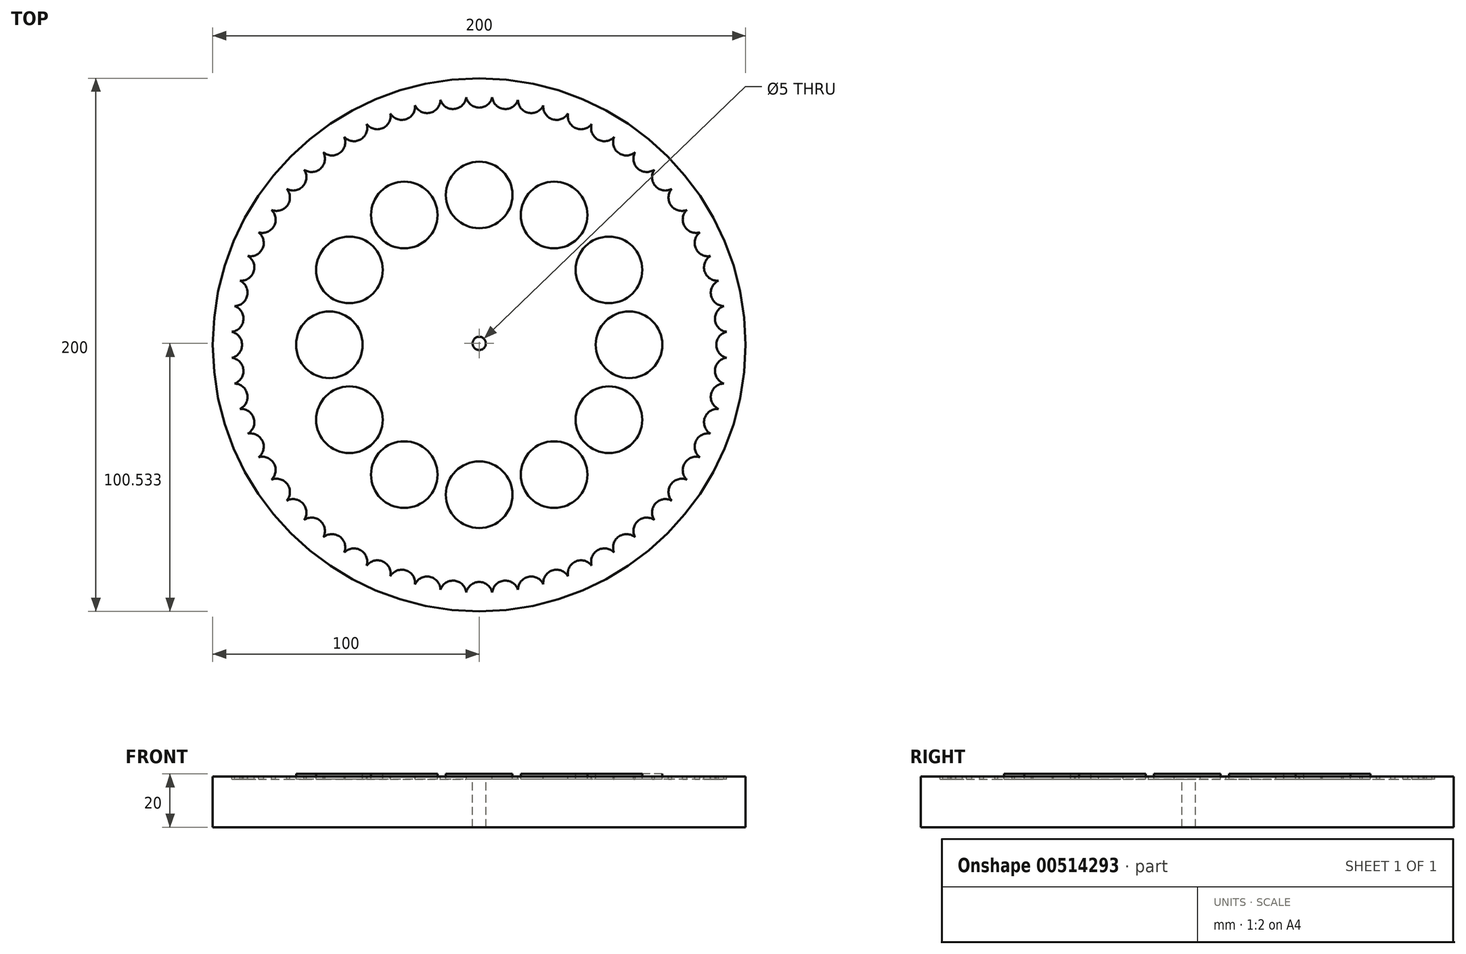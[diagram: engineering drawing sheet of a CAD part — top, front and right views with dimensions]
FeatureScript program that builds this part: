
annotation { "Feature Type Name" : "Feature", "Feature Type Description" : "" }
export const myFeature = defineFeature(function(context is Context, id is Id, definition is map)
    precondition{}
    {
        {
            var Q0;
            Q0=qCreatedBy(makeId("Top.planeOp"),FACE);
            var sketch = newSketch(context, id + "F0", { "sketchPlane" : qUnion([Q0])});
            skCircle(sketch, "E0", {"center": v(0, 0) * mm, "radius": 100 * mm});
            skSolve(sketch);
        }
        {
            var Q0;
            Q0=makeQuery(id+"F0.imprint","IMPRINT",FACE,{"disambiguationData":[TD([[makeQuery(id+"F0.imprint","IMPRINT",EDGE,{"derivedFrom":sQuery(id+"F0.wireOp",EDGE,"E0")}),1.0]])]});
            extrude(context, id + "F1", {"entities" : qUnion([Q0]), "oppositeDirection" : true, "depth" : 20 * mm});
        }
        {
            var Q0;
            Q0=makeQuery(id+"F1.opExtrude","CAP_FACE",FACE,{"disambiguationData":[OSD([sQuery(id+"F0.wireOp",EDGE,"E0")])],"isStart":true});
            var sketch = newSketch(context, id + "F2", { "sketchPlane" : qUnion([Q0])});
            skText(sketch, "E1", { "text": "12\n00", "fontName": "NotoSans-Regular.ttf"});
            skCircle(sketch, "E2", {"center": v(0, 56.24) * mm, "radius": 12.5 * mm});
            skCircle(sketch, "E3.1.0", {"center": v(-28.12, 48.7) * mm, "radius": 12.5 * mm});
            skCircle(sketch, "E3.2.0", {"center": v(-48.7, 28.12) * mm, "radius": 12.5 * mm});
            skCircle(sketch, "E3.3.0", {"center": v(-56.24, 0) * mm, "radius": 12.5 * mm});
            skCircle(sketch, "E3.4.0", {"center": v(-48.7, -28.12) * mm, "radius": 12.5 * mm});
            skCircle(sketch, "E3.5.0", {"center": v(-28.12, -48.7) * mm, "radius": 12.5 * mm});
            skCircle(sketch, "E3.6.0", {"center": v(0, -56.24) * mm, "radius": 12.5 * mm});
            skCircle(sketch, "E3.7.0", {"center": v(28.12, -48.7) * mm, "radius": 12.5 * mm});
            skCircle(sketch, "E3.8.0", {"center": v(48.7, -28.12) * mm, "radius": 12.5 * mm});
            skCircle(sketch, "E3.9.0", {"center": v(56.24, 0) * mm, "radius": 12.5 * mm});
            skCircle(sketch, "E3.10.0", {"center": v(48.7, 28.12) * mm, "radius": 12.5 * mm});
            skCircle(sketch, "E3.11.0", {"center": v(28.12, 48.7) * mm, "radius": 12.5 * mm});
            skPoint(sketch, "E3.center", {"position": v(0, 0) * mm});
            const initialGuessF2  = {"E1": [-0.00645, 0.06, 1, 0, 0.008]};
            skSetInitialGuess(sketch, initialGuessF2);
            skSolve(sketch);
        }
        {
            var Q0;
            Q0=makeQuery(id+"F2.imprint","IMPRINT",FACE,{"disambiguationData":[TD([[makeQuery(id+"F2.imprint","IMPRINT",EDGE,{"derivedFrom":sQuery(id+"F2.wireOp",EDGE,"E2")}),-1.0]])]});
            extrude(context, id + "F3", {"entities" : qUnion([Q0]), "operationType" : NewBodyOperationType.REMOVE, "oppositeDirection" : true, "depth" : 1 * mm});
        }
        {
            var Q0;
            Q0=makeQuery(id+"F3.boolean.opBoolean","COPY",FACE,{"derivedFrom":makeQuery(id+"F3.opExtrude","CAP_FACE",FACE,{"disambiguationData":[OSD([sQuery(id+"F0.wireOp",EDGE,"E0"),sQuery(id+"F2.wireOp",EDGE,"E2"),sQuery(id+"F2.wireOp",EDGE,"E3.1.0"),sQuery(id+"F2.wireOp",EDGE,"E3.2.0"),sQuery(id+"F2.wireOp",EDGE,"E3.3.0"),sQuery(id+"F2.wireOp",EDGE,"E3.4.0"),sQuery(id+"F2.wireOp",EDGE,"E3.5.0"),sQuery(id+"F2.wireOp",EDGE,"E3.6.0"),sQuery(id+"F2.wireOp",EDGE,"E3.7.0"),sQuery(id+"F2.wireOp",EDGE,"E3.8.0"),sQuery(id+"F2.wireOp",EDGE,"E3.9.0"),sQuery(id+"F2.wireOp",EDGE,"E3.10.0"),sQuery(id+"F2.wireOp",EDGE,"E3.11.0")])],"isStart":false})});
            var sketch = newSketch(context, id + "F4", { "sketchPlane" : qUnion([Q0])});
            skCircle(sketch, "E4", {"center": v(0, 94) * mm, "radius": 5 * mm});
            skCircle(sketch, "E5.1.0", {"center": v(-9.83, 93.49) * mm, "radius": 5 * mm});
            skCircle(sketch, "E5.2.0", {"center": v(-19.54, 91.95) * mm, "radius": 5 * mm});
            skCircle(sketch, "E5.3.0", {"center": v(-29.05, 89.4) * mm, "radius": 5 * mm});
            skCircle(sketch, "E5.4.0", {"center": v(-38.23, 85.87) * mm, "radius": 5 * mm});
            skCircle(sketch, "E5.5.0", {"center": v(-47, 81.4) * mm, "radius": 5 * mm});
            skCircle(sketch, "E5.6.0", {"center": v(-55.25, 76.05) * mm, "radius": 5 * mm});
            skCircle(sketch, "E5.7.0", {"center": v(-62.9, 69.86) * mm, "radius": 5 * mm});
            skCircle(sketch, "E5.8.0", {"center": v(-69.86, 62.9) * mm, "radius": 5 * mm});
            skCircle(sketch, "E5.9.0", {"center": v(-76.05, 55.25) * mm, "radius": 5 * mm});
            skCircle(sketch, "E5.10.0", {"center": v(-81.4, 47) * mm, "radius": 5 * mm});
            skCircle(sketch, "E5.11.0", {"center": v(-85.87, 38.23) * mm, "radius": 5 * mm});
            skCircle(sketch, "E5.12.0", {"center": v(-89.4, 29.05) * mm, "radius": 5 * mm});
            skCircle(sketch, "E5.13.0", {"center": v(-91.95, 19.54) * mm, "radius": 5 * mm});
            skCircle(sketch, "E5.14.0", {"center": v(-93.49, 9.83) * mm, "radius": 5 * mm});
            skCircle(sketch, "E5.15.0", {"center": v(-94, 0) * mm, "radius": 5 * mm});
            skCircle(sketch, "E5.16.0", {"center": v(-93.49, -9.83) * mm, "radius": 5 * mm});
            skCircle(sketch, "E5.17.0", {"center": v(-91.95, -19.54) * mm, "radius": 5 * mm});
            skCircle(sketch, "E5.18.0", {"center": v(-89.4, -29.05) * mm, "radius": 5 * mm});
            skCircle(sketch, "E5.19.0", {"center": v(-85.87, -38.23) * mm, "radius": 5 * mm});
            skCircle(sketch, "E5.20.0", {"center": v(-81.4, -47) * mm, "radius": 5 * mm});
            skCircle(sketch, "E5.21.0", {"center": v(-76.05, -55.25) * mm, "radius": 5 * mm});
            skCircle(sketch, "E5.22.0", {"center": v(-69.86, -62.9) * mm, "radius": 5 * mm});
            skCircle(sketch, "E5.23.0", {"center": v(-62.9, -69.86) * mm, "radius": 5 * mm});
            skCircle(sketch, "E5.24.0", {"center": v(-55.25, -76.05) * mm, "radius": 5 * mm});
            skCircle(sketch, "E5.25.0", {"center": v(-47, -81.4) * mm, "radius": 5 * mm});
            skCircle(sketch, "E5.26.0", {"center": v(-38.23, -85.87) * mm, "radius": 5 * mm});
            skCircle(sketch, "E5.27.0", {"center": v(-29.05, -89.4) * mm, "radius": 5 * mm});
            skCircle(sketch, "E5.28.0", {"center": v(-19.54, -91.95) * mm, "radius": 5 * mm});
            skCircle(sketch, "E5.29.0", {"center": v(-9.83, -93.49) * mm, "radius": 5 * mm});
            skCircle(sketch, "E5.30.0", {"center": v(0, -94) * mm, "radius": 5 * mm});
            skCircle(sketch, "E5.31.0", {"center": v(9.83, -93.49) * mm, "radius": 5 * mm});
            skCircle(sketch, "E5.32.0", {"center": v(19.54, -91.95) * mm, "radius": 5 * mm});
            skCircle(sketch, "E5.33.0", {"center": v(29.05, -89.4) * mm, "radius": 5 * mm});
            skCircle(sketch, "E5.34.0", {"center": v(38.23, -85.87) * mm, "radius": 5 * mm});
            skCircle(sketch, "E5.35.0", {"center": v(47, -81.4) * mm, "radius": 5 * mm});
            skCircle(sketch, "E5.36.0", {"center": v(55.25, -76.05) * mm, "radius": 5 * mm});
            skCircle(sketch, "E5.37.0", {"center": v(62.9, -69.86) * mm, "radius": 5 * mm});
            skCircle(sketch, "E5.38.0", {"center": v(69.86, -62.9) * mm, "radius": 5 * mm});
            skCircle(sketch, "E5.39.0", {"center": v(76.05, -55.25) * mm, "radius": 5 * mm});
            skCircle(sketch, "E5.40.0", {"center": v(81.4, -47) * mm, "radius": 5 * mm});
            skCircle(sketch, "E5.41.0", {"center": v(85.87, -38.23) * mm, "radius": 5 * mm});
            skCircle(sketch, "E5.42.0", {"center": v(89.4, -29.05) * mm, "radius": 5 * mm});
            skCircle(sketch, "E5.43.0", {"center": v(91.95, -19.54) * mm, "radius": 5 * mm});
            skCircle(sketch, "E5.44.0", {"center": v(93.49, -9.83) * mm, "radius": 5 * mm});
            skCircle(sketch, "E5.45.0", {"center": v(94, 0) * mm, "radius": 5 * mm});
            skCircle(sketch, "E5.46.0", {"center": v(93.49, 9.83) * mm, "radius": 5 * mm});
            skCircle(sketch, "E5.47.0", {"center": v(91.95, 19.54) * mm, "radius": 5 * mm});
            skCircle(sketch, "E5.48.0", {"center": v(89.4, 29.05) * mm, "radius": 5 * mm});
            skCircle(sketch, "E5.49.0", {"center": v(85.87, 38.23) * mm, "radius": 5 * mm});
            skCircle(sketch, "E5.50.0", {"center": v(81.4, 47) * mm, "radius": 5 * mm});
            skCircle(sketch, "E5.51.0", {"center": v(76.05, 55.25) * mm, "radius": 5 * mm});
            skCircle(sketch, "E5.52.0", {"center": v(69.86, 62.9) * mm, "radius": 5 * mm});
            skCircle(sketch, "E5.53.0", {"center": v(62.9, 69.86) * mm, "radius": 5 * mm});
            skCircle(sketch, "E5.54.0", {"center": v(55.25, 76.05) * mm, "radius": 5 * mm});
            skCircle(sketch, "E5.55.0", {"center": v(47, 81.4) * mm, "radius": 5 * mm});
            skCircle(sketch, "E5.56.0", {"center": v(38.23, 85.87) * mm, "radius": 5 * mm});
            skCircle(sketch, "E5.57.0", {"center": v(29.05, 89.4) * mm, "radius": 5 * mm});
            skCircle(sketch, "E5.58.0", {"center": v(19.54, 91.95) * mm, "radius": 5 * mm});
            skCircle(sketch, "E5.59.0", {"center": v(9.83, 93.49) * mm, "radius": 5 * mm});
            skPoint(sketch, "E5.center", {"position": v(0, 0) * mm});
            skSolve(sketch);
        }
        {
            var Q0;
            Q0=makeQuery(id+"F4.imprint","IMPRINT",FACE,{"disambiguationData":[TD([[makeQuery(id+"F4.imprint","IMPRINT",EDGE,{"derivedFrom":makeQuery(id+"F3.boolean.opBoolean","COPY",EDGE,{"derivedFrom":makeQuery(id+"F3.opExtrude","CAP_EDGE",EDGE,{"disambiguationData":[OSD([sQuery(id+"F2.wireOp",EDGE,"E2")])],"isStart":false})})}),-1.0]])]});
            var Q1;
            Q1=makeQuery(id+"F4.imprint","IMPRINT",FACE,{"disambiguationData":[TD([[makeQuery(id+"F4.imprint","IMPRINT",EDGE,{"derivedFrom":makeQuery(id+"F3.boolean.opBoolean","COPY",EDGE,{"derivedFrom":makeQuery(id+"F3.opExtrude","CAP_EDGE",EDGE,{"disambiguationData":[OSD([sQuery(id+"F0.wireOp",EDGE,"E0")])],"isStart":false})})}),1.0]])]});
            extrude(context, id + "F5", {"entities" : qUnion([Q0, Q1]), "operationType" : NewBodyOperationType.REMOVE, "oppositeDirection" : true, "depth" : 1 * mm});
        }
        {
            var Q0;
            Q0=makeQuery(id+"F5.boolean.opBoolean","COPY",FACE,{"derivedFrom":makeQuery(id+"F5.opExtrude","CAP_FACE",FACE,{"disambiguationData":[OSD([sQuery(id+"F2.wireOp",EDGE,"E2"),sQuery(id+"F2.wireOp",EDGE,"E3.1.0"),sQuery(id+"F2.wireOp",EDGE,"E3.2.0"),sQuery(id+"F2.wireOp",EDGE,"E3.3.0"),sQuery(id+"F2.wireOp",EDGE,"E3.4.0"),sQuery(id+"F2.wireOp",EDGE,"E3.5.0"),sQuery(id+"F2.wireOp",EDGE,"E3.6.0"),sQuery(id+"F2.wireOp",EDGE,"E3.7.0"),sQuery(id+"F2.wireOp",EDGE,"E3.8.0"),sQuery(id+"F2.wireOp",EDGE,"E3.9.0"),sQuery(id+"F2.wireOp",EDGE,"E3.10.0"),sQuery(id+"F2.wireOp",EDGE,"E3.11.0"),sQuery(id+"F4.wireOp",EDGE,"E4"),sQuery(id+"F4.wireOp",EDGE,"E5.1.0"),sQuery(id+"F4.wireOp",EDGE,"E5.2.0"),sQuery(id+"F4.wireOp",EDGE,"E5.3.0"),sQuery(id+"F4.wireOp",EDGE,"E5.4.0"),sQuery(id+"F4.wireOp",EDGE,"E5.5.0"),sQuery(id+"F4.wireOp",EDGE,"E5.6.0"),sQuery(id+"F4.wireOp",EDGE,"E5.7.0"),sQuery(id+"F4.wireOp",EDGE,"E5.8.0"),sQuery(id+"F4.wireOp",EDGE,"E5.9.0"),sQuery(id+"F4.wireOp",EDGE,"E5.10.0"),sQuery(id+"F4.wireOp",EDGE,"E5.11.0"),sQuery(id+"F4.wireOp",EDGE,"E5.12.0"),sQuery(id+"F4.wireOp",EDGE,"E5.13.0"),sQuery(id+"F4.wireOp",EDGE,"E5.14.0"),sQuery(id+"F4.wireOp",EDGE,"E5.15.0"),sQuery(id+"F4.wireOp",EDGE,"E5.16.0"),sQuery(id+"F4.wireOp",EDGE,"E5.17.0"),sQuery(id+"F4.wireOp",EDGE,"E5.18.0"),sQuery(id+"F4.wireOp",EDGE,"E5.19.0"),sQuery(id+"F4.wireOp",EDGE,"E5.20.0"),sQuery(id+"F4.wireOp",EDGE,"E5.21.0"),sQuery(id+"F4.wireOp",EDGE,"E5.22.0"),sQuery(id+"F4.wireOp",EDGE,"E5.23.0"),sQuery(id+"F4.wireOp",EDGE,"E5.24.0"),sQuery(id+"F4.wireOp",EDGE,"E5.25.0"),sQuery(id+"F4.wireOp",EDGE,"E5.26.0"),sQuery(id+"F4.wireOp",EDGE,"E5.27.0"),sQuery(id+"F4.wireOp",EDGE,"E5.28.0"),sQuery(id+"F4.wireOp",EDGE,"E5.29.0"),sQuery(id+"F4.wireOp",EDGE,"E5.30.0"),sQuery(id+"F4.wireOp",EDGE,"E5.31.0"),sQuery(id+"F4.wireOp",EDGE,"E5.32.0"),sQuery(id+"F4.wireOp",EDGE,"E5.33.0"),sQuery(id+"F4.wireOp",EDGE,"E5.34.0"),sQuery(id+"F4.wireOp",EDGE,"E5.35.0"),sQuery(id+"F4.wireOp",EDGE,"E5.36.0"),sQuery(id+"F4.wireOp",EDGE,"E5.37.0"),sQuery(id+"F4.wireOp",EDGE,"E5.38.0"),sQuery(id+"F4.wireOp",EDGE,"E5.39.0"),sQuery(id+"F4.wireOp",EDGE,"E5.40.0"),sQuery(id+"F4.wireOp",EDGE,"E5.41.0"),sQuery(id+"F4.wireOp",EDGE,"E5.42.0"),sQuery(id+"F4.wireOp",EDGE,"E5.43.0"),sQuery(id+"F4.wireOp",EDGE,"E5.44.0"),sQuery(id+"F4.wireOp",EDGE,"E5.45.0"),sQuery(id+"F4.wireOp",EDGE,"E5.46.0"),sQuery(id+"F4.wireOp",EDGE,"E5.47.0"),sQuery(id+"F4.wireOp",EDGE,"E5.48.0"),sQuery(id+"F4.wireOp",EDGE,"E5.49.0"),sQuery(id+"F4.wireOp",EDGE,"E5.50.0"),sQuery(id+"F4.wireOp",EDGE,"E5.51.0"),sQuery(id+"F4.wireOp",EDGE,"E5.52.0"),sQuery(id+"F4.wireOp",EDGE,"E5.53.0"),sQuery(id+"F4.wireOp",EDGE,"E5.54.0"),sQuery(id+"F4.wireOp",EDGE,"E5.55.0"),sQuery(id+"F4.wireOp",EDGE,"E5.56.0"),sQuery(id+"F4.wireOp",EDGE,"E5.57.0"),sQuery(id+"F4.wireOp",EDGE,"E5.58.0"),sQuery(id+"F4.wireOp",EDGE,"E5.59.0")])],"isStart":false})});
            var sketch = newSketch(context, id + "F6", { "sketchPlane" : qUnion([Q0])});
            skCircle(sketch, "E6", {"center": v(0, 0.53) * mm, "radius": 2.5 * mm});
            skSolve(sketch);
        }
        {
            var Q0;
            Q0 = qSketchRegion(id + "F6", true);
            extrude(context, id + "F7", {"entities" : qUnion([Q0]), "operationType" : NewBodyOperationType.REMOVE, "oppositeDirection" : true, "depth" : 25 * mm});
        }
    });
